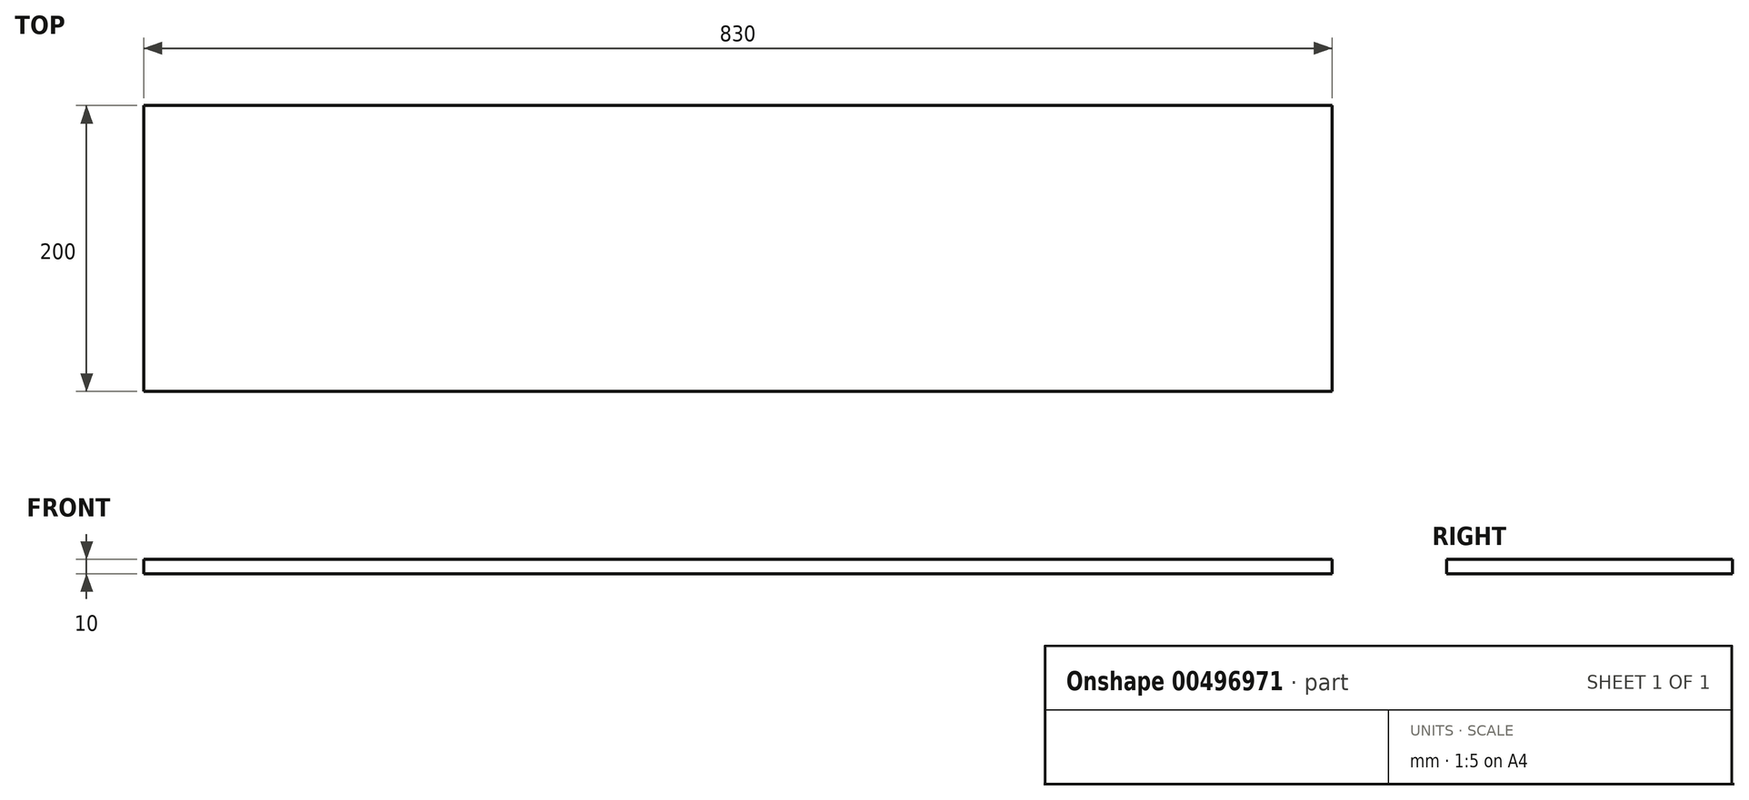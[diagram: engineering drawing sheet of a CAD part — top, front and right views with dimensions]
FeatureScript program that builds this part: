
annotation { "Feature Type Name" : "Feature", "Feature Type Description" : "" }
export const myFeature = defineFeature(function(context is Context, id is Id, definition is map)
    precondition{}
    {
        {
            var Q0;
            Q0=qCreatedBy(makeId("Top.planeOp"),FACE);
            var sketch = newSketch(context, id + "F0", { "sketchPlane" : qUnion([Q0])});
            skLineSegment(sketch, "E0.bottom", {"start": v(415, -100) * mm, "end": v(-415, -100) * mm});
            skLineSegment(sketch, "E0.top", {"start": v(415, 100) * mm, "end": v(-415, 100) * mm});
            skLineSegment(sketch, "E0.left", {"start": v(415, -100) * mm, "end": v(415, 100) * mm});
            skLineSegment(sketch, "E0.right", {"start": v(-415, -100) * mm, "end": v(-415, 100) * mm});
            skPoint(sketch, "E0.middle", {"position": v(0, 0) * mm});
            skSolve(sketch);
        }
        {
            var Q0;
            Q0 = qSketchRegion(id + "F0", true);
            extrude(context, id + "F1", {"entities" : qUnion([Q0]), "depth" : 10 * mm});
        }
    });
